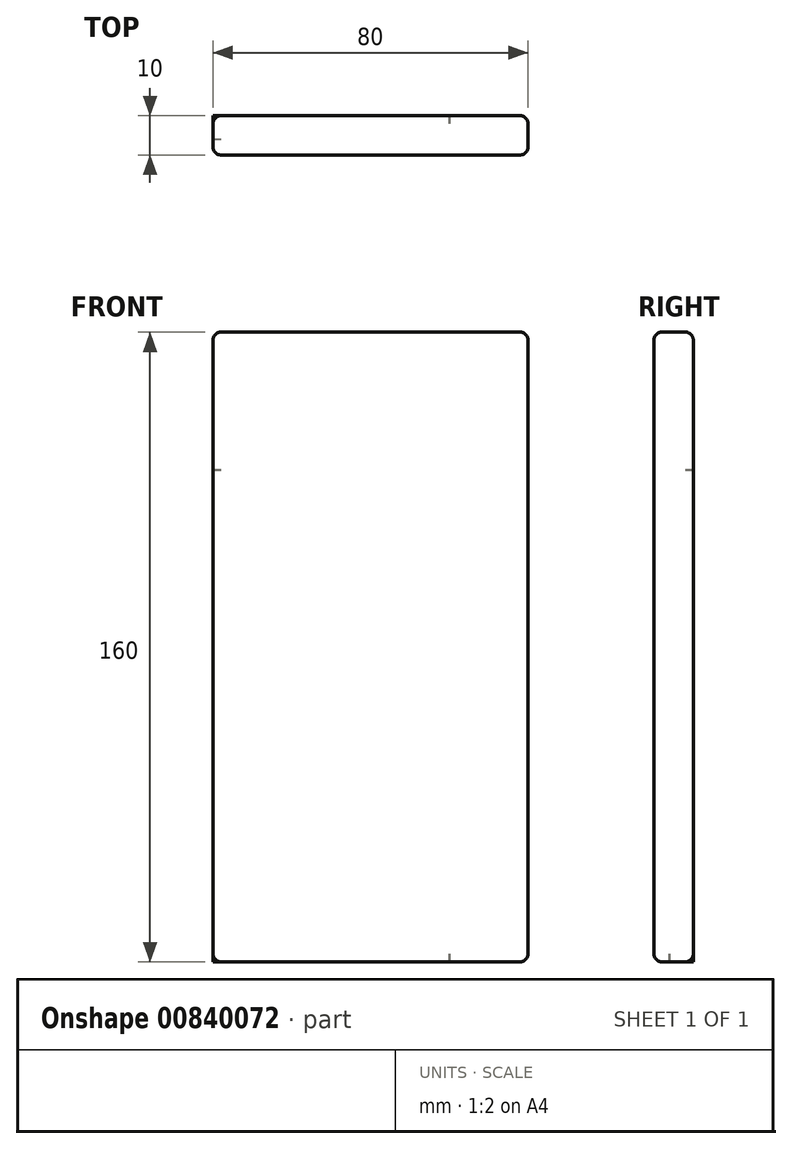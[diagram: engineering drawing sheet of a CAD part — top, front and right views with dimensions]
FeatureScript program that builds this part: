
annotation { "Feature Type Name" : "Feature", "Feature Type Description" : "" }
export const myFeature = defineFeature(function(context is Context, id is Id, definition is map)
    precondition{}
    {
        {
            var Q0;
            Q0=qCreatedBy(makeId("Front.planeOp"),FACE);
            var sketch = newSketch(context, id + "F0", { "sketchPlane" : qUnion([Q0])});
            skLineSegment(sketch, "E0.bottom", {"start": v(0, 0) * mm, "end": v(80, 0) * mm});
            skLineSegment(sketch, "E0.top", {"start": v(0, 160) * mm, "end": v(80, 160) * mm});
            skLineSegment(sketch, "E0.left", {"start": v(0, 0) * mm, "end": v(0, 160) * mm});
            skLineSegment(sketch, "E0.right", {"start": v(80, 0) * mm, "end": v(80, 160) * mm});
            skSolve(sketch);
        }
        {
            var Q0;
            Q0 = qSketchRegion(id + "F0", true);
            extrude(context, id + "F1", {"entities" : qUnion([Q0]), "depth" : 10 * mm, "offsetDistance" : 25 * mm});
        }
        {
            var Q0;
            Q0=makeQuery(id+"F1.opExtrude","CAP_EDGE",EDGE,{"disambiguationData":[OSD([sQuery(id+"F0.wireOp",EDGE,"E0.right")])],"isStart":false});
            var Q1;
            Q1=makeQuery(id+"F1.opExtrude","CAP_EDGE",EDGE,{"disambiguationData":[OSD([sQuery(id+"F0.wireOp",EDGE,"E0.top")])],"isStart":false});
            var Q2;
            Q2=makeQuery(id+"F1.opExtrude","CAP_EDGE",EDGE,{"disambiguationData":[OSD([sQuery(id+"F0.wireOp",EDGE,"E0.left")])],"isStart":false});
            var Q3;
            Q3=makeQuery(id+"F1.opExtrude","CAP_EDGE",EDGE,{"disambiguationData":[OSD([sQuery(id+"F0.wireOp",EDGE,"E0.bottom")])],"isStart":false});
            var Q4;
            Q4=makeQuery(id+"F1.opExtrude","SWEPT_EDGE",EDGE,{"disambiguationData":[OSD([sQuery(id+"F0.wireOp",EDGE,"E0.top"),sQuery(id+"F0.wireOp",EDGE,"E0.left")])]});
            var Q5;
            Q5=makeQuery(id+"F1.opExtrude","SWEPT_EDGE",EDGE,{"disambiguationData":[OSD([sQuery(id+"F0.wireOp",EDGE,"E0.top"),sQuery(id+"F0.wireOp",EDGE,"E0.right")])]});
            var Q6;
            Q6=makeQuery(id+"F1.opExtrude","SWEPT_EDGE",EDGE,{"disambiguationData":[OSD([sQuery(id+"F0.wireOp",EDGE,"E0.bottom"),sQuery(id+"F0.wireOp",EDGE,"E0.right")])]});
            var Q7;
            Q7=makeQuery(id+"F1.opExtrude","SWEPT_EDGE",EDGE,{"disambiguationData":[OSD([sQuery(id+"F0.wireOp",EDGE,"E0.bottom"),sQuery(id+"F0.wireOp",EDGE,"E0.left")])]});
            var Q8;
            Q8=makeQuery(id+"F1.opExtrude","CAP_EDGE",EDGE,{"disambiguationData":[OSD([sQuery(id+"F0.wireOp",EDGE,"E0.bottom")])],"isStart":true});
            var Q9;
            Q9=makeQuery(id+"F1.opExtrude","CAP_EDGE",EDGE,{"disambiguationData":[OSD([sQuery(id+"F0.wireOp",EDGE,"E0.right")])],"isStart":true});
            var Q10;
            Q10=makeQuery(id+"F1.opExtrude","CAP_EDGE",EDGE,{"disambiguationData":[OSD([sQuery(id+"F0.wireOp",EDGE,"E0.top")])],"isStart":true});
            var Q11;
            Q11=makeQuery(id+"F1.opExtrude","CAP_EDGE",EDGE,{"disambiguationData":[OSD([sQuery(id+"F0.wireOp",EDGE,"E0.left")])],"isStart":true});
            fillet(context, id + "F2", {"entities" : qUnion([Q0, Q1, Q2, Q3, Q4, Q5, Q6, Q7, Q8, Q9, Q10, Q11]), "radius" : 2 * mm, "tangentPropagation" : true, "allowEdgeOverflow" : false});
        }
        {
            var Q0;
            Q0=qCreatedBy(makeId("Front.planeOp"),FACE);
            var sketch = newSketch(context, id + "F3", { "sketchPlane" : qUnion([Q0])});
            skLineSegment(sketch, "E1.bottom", {"start": v(0, 0) * mm, "end": v(60, 0) * mm});
            skLineSegment(sketch, "E1.top", {"start": v(0, 125) * mm, "end": v(60, 125) * mm});
            skLineSegment(sketch, "E1.left", {"start": v(0, 0) * mm, "end": v(0, 125) * mm});
            skLineSegment(sketch, "E1.right", {"start": v(60, 0) * mm, "end": v(60, 125) * mm});
            skSolve(sketch);
        }
        {
            var Q0;
            Q0 = qSketchRegion(id + "F3", true);
            extrude(context, id + "F4", {"entities" : qUnion([Q0]), "operationType" : NewBodyOperationType.ADD, "depth" : 6 * mm, "offsetDistance" : 25 * mm});
        }
    });
